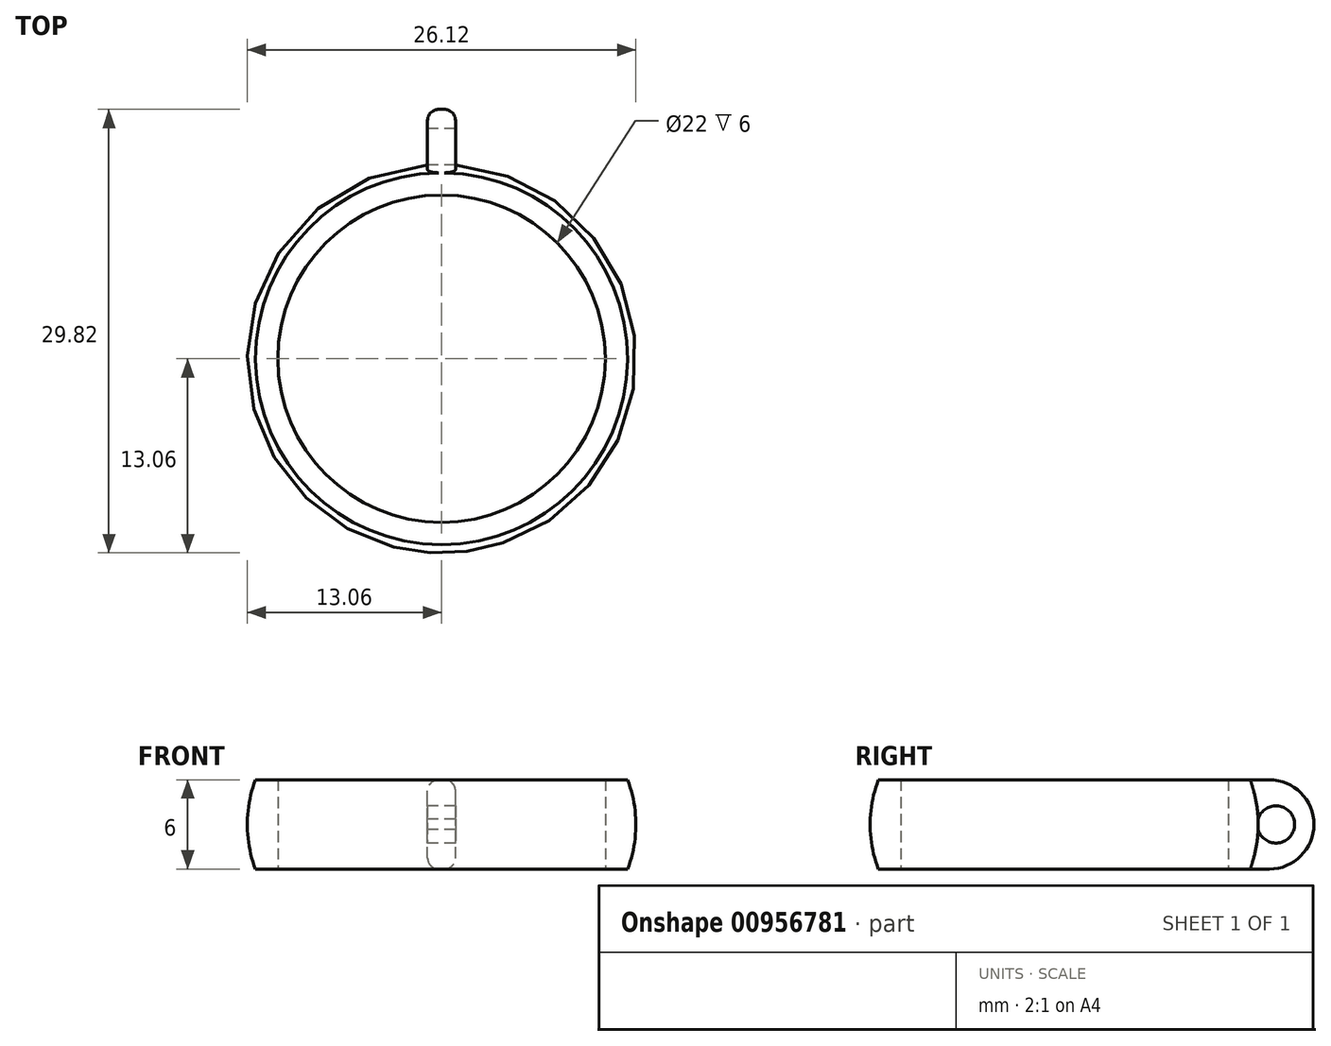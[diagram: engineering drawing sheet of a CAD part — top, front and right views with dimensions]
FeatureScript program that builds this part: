
annotation { "Feature Type Name" : "Feature", "Feature Type Description" : "" }
export const myFeature = defineFeature(function(context is Context, id is Id, definition is map)
    precondition{}
    {
        {
            var Q0;
            Q0=qCreatedBy(makeId("Front.planeOp"),FACE);
            var sketch = newSketch(context, id + "F0", { "sketchPlane" : qUnion([Q0])});
            skLineSegment(sketch, "E0", {"start": v(0, 0) * mm, "end": v(-11, 0) * mm});
            skLineSegment(sketch, "E1.bottom", {"start": v(-11, 3) * mm, "end": v(-11, 3) * mm});
            skLineSegment(sketch, "E1.top", {"start": v(-11, -3) * mm, "end": v(-11, -3) * mm});
            skLineSegment(sketch, "E1.left", {"start": v(-11, 3) * mm, "end": v(-11, -3) * mm});
            skLineSegment(sketch, "E1.right", {"start": v(-11, 3) * mm, "end": v(-11, -3) * mm});
            skPoint(sketch, "E1.middle", {"position": v(-11, 0) * mm});
            skLineSegment(sketch, "E2.bottom", {"start": v(-11, 3) * mm, "end": v(-12.5, 3) * mm});
            skLineSegment(sketch, "E2.top", {"start": v(-11, -3) * mm, "end": v(-12.5, -3) * mm});
            skArc(sketch, "E3", {"start": v(-12.5, 3) * mm, "mid": v(-13.06, 0) * mm, "end": v(-12.5, -3) * mm});
            skLineSegment(sketch, "E4", {"start": v(0, 0) * mm, "end": v(0, 3.85) * mm});
            skSolve(sketch);
        }
        {
            var Q0;
            {var subQ3=sQuery(id+"F0.wireOp",EDGE,"E2.bottom");Q0=makeQuery(id+"F0.imprint","IMPRINT",FACE,{"disambiguationData":[TD([[makeQuery(id+"F0.imprint","IMPRINT",EDGE,{"derivedFrom":subQ3}),1.0]])]});}
            var Q1;
            Q1=sQuery(id+"F0.wireOp",EDGE,"E4");
            revolve(context, id + "F1", {"surfaceOperationType" : NewSurfaceOperationType.NEW, "entities" : qUnion([Q0]), "axis" : qUnion([Q1]), "revolveType" : RevolveType.FULL});
        }
        {
            var Q0;
            Q0=qCreatedBy(makeId("Top.planeOp"),FACE);
            var sketch = newSketch(context, id + "F2", { "sketchPlane" : qUnion([Q0])});
            skLineSegment(sketch, "E5.bottom", {"start": v(0.94, 16.76) * mm, "end": v(-0.94, 16.76) * mm});
            skLineSegment(sketch, "E5.left", {"start": v(0.94, 16.76) * mm, "end": v(0.94, 12.46) * mm});
            skLineSegment(sketch, "E5.right", {"start": v(-0.94, 16.76) * mm, "end": v(-0.94, 12.46) * mm});
            skPoint(sketch, "E5.middle", {"position": v(0, 11.76) * mm});
            skCircle(sketch, "E6", {"center": v(0, 0) * mm, "radius": 12.5 * mm});
            skPoint(sketch, "E5.top.end.orphan", {"position": v(-0.94, 6.76) * mm});
            skPoint(sketch, "E5.top.start.orphan", {"position": v(0.94, 6.76) * mm});
            skSolve(sketch);
        }
        {
            var Q0;
            Q0=makeQuery(id+"F2.imprint","IMPRINT",FACE,{"disambiguationData":[TD([[makeQuery(id+"F2.imprint","IMPRINT",EDGE,{"derivedFrom":sQuery(id+"F2.wireOp",EDGE,"E5.bottom")}),1.0]])]});
            extrude(context, id + "F3", {"entities" : qUnion([Q0]), "operationType" : NewBodyOperationType.ADD, "depth" : 3 * mm, "offsetDistance" : 25 * mm});
        }
        {
            var Q0;
            Q0=makeQuery(id+"F3.opExtrude","CAP_FACE",FACE,{"disambiguationData":[OSD([sQuery(id+"F2.wireOp",EDGE,"E5.bottom"),sQuery(id+"F2.wireOp",EDGE,"E5.left"),sQuery(id+"F2.wireOp",EDGE,"E5.right"),sQuery(id+"F2.wireOp",EDGE,"E6")])],"isStart":true});
            var Q1;
            Q1 = qSketchRegion(id + "F2", true);
            extrude(context, id + "F4", {"entities" : qUnion([Q0, Q1]), "operationType" : NewBodyOperationType.ADD, "depth" : 3 * mm, "offsetDistance" : 25 * mm});
        }
        {
            var Q0;
            Q0=makeQuery(id+"F3.opExtrude","CAP_EDGE",EDGE,{"disambiguationData":[OSD([sQuery(id+"F2.wireOp",EDGE,"E5.bottom")])],"isStart":false});
            var Q1;
            {var subQ0=sQuery(id+"F2.wireOp",EDGE,"E5.bottom");Q1=makeQuery(id+"F4.opExtrude","CAP_EDGE",EDGE,{"disambiguationData":[OSD([subQ0]),TDD([makeQuery(id+"F2.imprint","IMPRINT",EDGE,{"derivedFrom":subQ0})])],"isStart":false});}
            fillet(context, id + "F5", {"entities" : qUnion([Q0, Q1]), "radius" : 3 * mm, "tangentPropagation" : true, "allowEdgeOverflow" : false});
        }
        {
            var Q0;
            {var subQ0=sQuery(id+"F2.wireOp",EDGE,"E5.left");Q0=makeQuery(id+"F4.opExtrude","CAP_EDGE",EDGE,{"disambiguationData":[OSD([subQ0]),TDD([makeQuery(id+"F2.imprint","IMPRINT",EDGE,{"derivedFrom":subQ0})])],"isStart":false});}
            var Q1;
            {var subQ0=sQuery(id+"F2.wireOp",EDGE,"E5.left");Q1=makeQuery(id+"F5.opFillet","BLEND_EDGE",EDGE,{"blendedFrom":[makeQuery(id+"F3.opExtrude","CAP_EDGE",EDGE,{"disambiguationData":[OSD([sQuery(id+"F2.wireOp",EDGE,"E5.bottom")])],"isStart":false}),makeQuery(id+"F4.boolean.opBoolean","MERGE",FACE,{"derivedFrom":[makeQuery(id+"F3.opExtrude","SWEPT_FACE",FACE,{"disambiguationData":[OSD([subQ0])]}),makeQuery(id+"F4.opExtrude","SWEPT_FACE",FACE,{"disambiguationData":[OSD([subQ0]),TDD([makeQuery(id+"F2.imprint","IMPRINT",EDGE,{"derivedFrom":subQ0})])]})]})],"blendedInto":[makeQuery(id+"F4.boolean.opBoolean","MERGE",FACE,{"derivedFrom":[makeQuery(id+"F3.opExtrude","SWEPT_FACE",FACE,{"disambiguationData":[OSD([subQ0])]}),makeQuery(id+"F4.opExtrude","SWEPT_FACE",FACE,{"disambiguationData":[OSD([subQ0]),TDD([makeQuery(id+"F2.imprint","IMPRINT",EDGE,{"derivedFrom":subQ0})])]})]})]});}
            var Q2;
            {var subQ0=sQuery(id+"F2.wireOp",EDGE,"E5.right");Q2=makeQuery(id+"F5.opFillet","BLEND_EDGE",EDGE,{"blendedFrom":[makeQuery(id+"F3.opExtrude","CAP_EDGE",EDGE,{"disambiguationData":[OSD([sQuery(id+"F2.wireOp",EDGE,"E5.bottom")])],"isStart":false}),makeQuery(id+"F4.boolean.opBoolean","MERGE",FACE,{"derivedFrom":[makeQuery(id+"F3.opExtrude","SWEPT_FACE",FACE,{"disambiguationData":[OSD([subQ0])]}),makeQuery(id+"F4.opExtrude","SWEPT_FACE",FACE,{"disambiguationData":[OSD([subQ0]),TDD([makeQuery(id+"F2.imprint","IMPRINT",EDGE,{"derivedFrom":subQ0})])]})]})],"blendedInto":[makeQuery(id+"F4.boolean.opBoolean","MERGE",FACE,{"derivedFrom":[makeQuery(id+"F3.opExtrude","SWEPT_FACE",FACE,{"disambiguationData":[OSD([subQ0])]}),makeQuery(id+"F4.opExtrude","SWEPT_FACE",FACE,{"disambiguationData":[OSD([subQ0]),TDD([makeQuery(id+"F2.imprint","IMPRINT",EDGE,{"derivedFrom":subQ0})])]})]})]});}
            var Q3;
            Q3=makeQuery(id+"F3.opExtrude","CAP_EDGE",EDGE,{"disambiguationData":[OSD([sQuery(id+"F2.wireOp",EDGE,"E5.right")])],"isStart":false});
            var Q4;
            {var subQ0=sQuery(id+"F2.wireOp",EDGE,"E5.right");Q4=makeQuery(id+"F4.opExtrude","CAP_EDGE",EDGE,{"disambiguationData":[OSD([subQ0]),TDD([makeQuery(id+"F2.imprint","IMPRINT",EDGE,{"derivedFrom":subQ0})])],"isStart":false});}
            fillet(context, id + "F6", {"entities" : qUnion([Q0, Q1, Q2, Q3, Q4]), "radius" : 0.75 * mm, "tangentPropagation" : true, "allowEdgeOverflow" : false});
        }
        {
            var Q0;
            {var subQ0=sQuery(id+"F2.wireOp",EDGE,"E5.right");Q0=makeQuery(id+"F4.boolean.opBoolean","MERGE",FACE,{"derivedFrom":[makeQuery(id+"F3.opExtrude","SWEPT_FACE",FACE,{"disambiguationData":[OSD([subQ0])]}),makeQuery(id+"F4.opExtrude","SWEPT_FACE",FACE,{"disambiguationData":[OSD([subQ0]),TDD([makeQuery(id+"F2.imprint","IMPRINT",EDGE,{"derivedFrom":subQ0})])]})]});}
            var sketch = newSketch(context, id + "F7", { "sketchPlane" : qUnion([Q0])});
            skCircle(sketch, "E7", {"center": v(-14.21, 0) * mm, "radius": 1.25 * mm});
            skSolve(sketch);
        }
        {
            var Q0;
            {var subQ0=sQuery(id+"F7.wireOp",EDGE,"E7");var subQ1=sQuery(id+"F2.wireOp",EDGE,"E5.right");var subQ2=makeQuery(id+"F4.boolean.opBoolean","INTERSECT",EDGE,{"derivedFrom":[makeQuery(id+"F1.opRevolve","SWEPT_FACE",FACE,{"disambiguationData":[OSD([sQuery(id+"F0.wireOp",EDGE,"E3")])]}),makeQuery(id+"F4.opExtrude","SWEPT_FACE",FACE,{"disambiguationData":[OSD([subQ1]),TDD([makeQuery(id+"F2.imprint","IMPRINT",EDGE,{"derivedFrom":subQ1})])]})]});var subQ3=makeQuery(id+"F7.imprint","INTERSECT",VERTEX,{"disambiguationData":[OD(0.0)],"derivedFrom":[subQ2,subQ0]});Q0=makeQuery(id+"F7.imprint","IMPRINT",FACE,{"disambiguationData":[TD([[makeQuery(id+"F7.imprint","IMPRINT",EDGE,{"disambiguationData":[TD([[subQ3,-1.0]])],"derivedFrom":subQ0}),1.0]])]});}
            extrude(context, id + "F8", {"entities" : qUnion([Q0]), "operationType" : NewBodyOperationType.REMOVE, "oppositeDirection" : true, "depth" : 2 * mm, "offsetDistance" : 25 * mm});
        }
        {
            var Q0;
            {var subQ0=sQuery(id+"F2.wireOp",EDGE,"E6");var subQ1=makeQuery(id+"F2.imprint","INTERSECT",VERTEX,{"derivedFrom":[sQuery(id+"F2.wireOp",EDGE,"E5.left"),subQ0]});Q0=makeQuery(id+"F2.imprint","IMPRINT",FACE,{"disambiguationData":[TD([[makeQuery(id+"F2.imprint","IMPRINT",EDGE,{"disambiguationData":[TD([[subQ1,-1.0]])],"derivedFrom":subQ0}),1.0]])]});}
            var sketch = newSketch(context, id + "F9", { "sketchPlane" : qUnion([Q0])});
            skCircle(sketch, "E8", {"center": v(0, 0) * mm, "radius": 11 * mm});
            skSolve(sketch);
        }
        {
            var Q0;
            Q0 = qSketchRegion(id + "F9", true);
            extrude(context, id + "F10", {"entities" : qUnion([Q0]), "operationType" : NewBodyOperationType.REMOVE, "oppositeDirection" : true, "depth" : 25 * mm, "offsetDistance" : 25 * mm});
        }
    });
